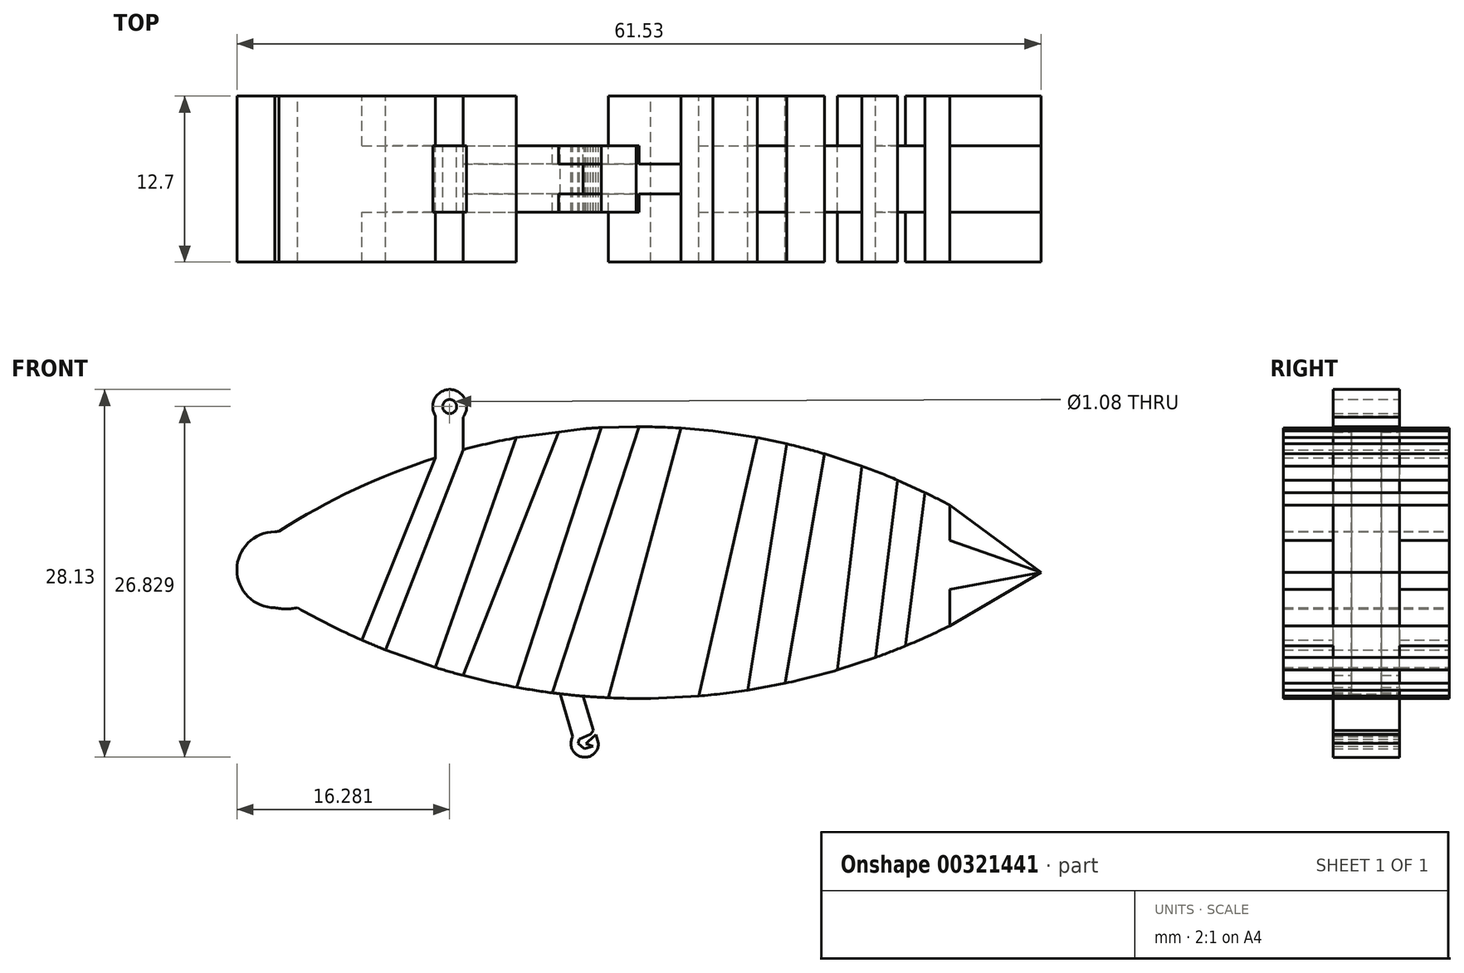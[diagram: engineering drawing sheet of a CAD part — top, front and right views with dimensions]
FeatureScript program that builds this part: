
annotation { "Feature Type Name" : "Feature", "Feature Type Description" : "" }
export const myFeature = defineFeature(function(context is Context, id is Id, definition is map)
    precondition{}
    {
        {
            var Q0;
            Q0=qCreatedBy(makeId("Front.planeOp"),FACE);
            var sketch = newSketch(context, id + "F0", { "sketchPlane" : qUnion([Q0])});
            skPoint(sketch, "E0", {"position": v(-30.3, 18.79) * mm});
            skPoint(sketch, "E1", {"position": v(21.02, 20.78) * mm});
            skArc(sketch, "E2", {"start": v(21.02, 20.78) * mm, "mid": v(-4.92, 26.75) * mm, "end": v(-30.3, 18.79) * mm});
            skPoint(sketch, "E3", {"position": v(-30.63, 18.74) * mm});
            skPoint(sketch, "E4", {"position": v(-30.63, 12.94) * mm});
            skPoint(sketch, "E5", {"position": v(-28.9, 12.94) * mm});
            skPoint(sketch, "E6", {"position": v(21.02, 11.56) * mm});
            skArc(sketch, "E7", {"start": v(-28.9, 12.94) * mm, "mid": v(-4.11, 6.01) * mm, "end": v(21.02, 11.56) * mm});
            skArc(sketch, "E8", {"start": v(-30.3, 18.79) * mm, "mid": v(-30.47, 18.77) * mm, "end": v(-30.63, 18.74) * mm});
            skArc(sketch, "E9", {"start": v(-30.63, 18.74) * mm, "mid": v(-33.53, 15.84) * mm, "end": v(-30.63, 12.94) * mm});
            skArc(sketch, "E10", {"start": v(-30.63, 12.94) * mm, "mid": v(-29.76, 12.85) * mm, "end": v(-28.9, 12.94) * mm});
            skPoint(sketch, "E11", {"position": v(28, 15.63) * mm});
            skLineSegment(sketch, "E12", {"start": v(21.02, 20.78) * mm, "end": v(28, 15.63) * mm});
            skLineSegment(sketch, "E13", {"start": v(28, 15.63) * mm, "end": v(28, 15.63) * mm});
            skLineSegment(sketch, "E14", {"start": v(28, 15.63) * mm, "end": v(21.02, 11.56) * mm});
            skPoint(sketch, "E15", {"position": v(18.72, 6.75) * mm});
            skLineSegment(sketch, "E16", {"start": v(-18.34, 24.4) * mm, "end": v(-18.34, 27.63) * mm});
            skLineSegment(sketch, "E17", {"start": v(-18.34, 27.63) * mm, "end": v(-16.23, 27.52) * mm});
            skLineSegment(sketch, "E18", {"start": v(-16.23, 27.52) * mm, "end": v(-16.23, 25.02) * mm});
            skArc(sketch, "E19", {"start": v(-16.23, 27.52) * mm, "mid": v(-17.18, 29.63) * mm, "end": v(-18.34, 27.63) * mm});
            skCircle(sketch, "E20", {"center": v(-17.25, 28.33) * mm, "radius": 0.54 * mm});
            skLineSegment(sketch, "E21", {"start": v(-23.96, 10.46) * mm, "end": v(-18.34, 24.4) * mm});
            skLineSegment(sketch, "E22", {"start": v(-16.23, 25.02) * mm, "end": v(-22.14, 9.7) * mm});
            skLineSegment(sketch, "E23", {"start": v(-22.14, 9.7) * mm, "end": v(-18.34, 8.37) * mm});
            skLineSegment(sketch, "E24", {"start": v(-18.34, 8.37) * mm, "end": v(-12.16, 25.94) * mm});
            skLineSegment(sketch, "E25", {"start": v(-12.16, 25.94) * mm, "end": v(-7.04, 26.62) * mm});
            skLineSegment(sketch, "E26", {"start": v(-16.23, 7.76) * mm, "end": v(-12.16, 6.69) * mm});
            skLineSegment(sketch, "E27", {"start": v(-12.16, 6.69) * mm, "end": v(-5.66, 26.72) * mm});
            skLineSegment(sketch, "E28", {"start": v(-5.66, 26.72) * mm, "end": v(-2.97, 26.79) * mm});
            skLineSegment(sketch, "E29", {"start": v(-7.04, 6.18) * mm, "end": v(-7.04, 6.18) * mm});
            skLineSegment(sketch, "E30", {"start": v(0, 26.72) * mm, "end": v(2.88, 26.45) * mm});
            skLineSegment(sketch, "E31", {"start": v(2.88, 26.45) * mm, "end": v(-1.88, 6) * mm});
            skLineSegment(sketch, "E32", {"start": v(-1.88, 6) * mm, "end": v(1.8, 6.18) * mm});
            skLineSegment(sketch, "E33", {"start": v(1.8, 6.18) * mm, "end": v(6.28, 25.94) * mm});
            skLineSegment(sketch, "E34", {"start": v(6.28, 25.94) * mm, "end": v(8.55, 25.47) * mm});
            skLineSegment(sketch, "E35", {"start": v(8.55, 25.47) * mm, "end": v(5.56, 6.63) * mm});
            skLineSegment(sketch, "E36", {"start": v(5.56, 6.63) * mm, "end": v(8.41, 7.16) * mm});
            skLineSegment(sketch, "E37", {"start": v(8.41, 7.16) * mm, "end": v(11.43, 24.71) * mm});
            skLineSegment(sketch, "E38", {"start": v(11.43, 24.71) * mm, "end": v(14.29, 23.78) * mm});
            skLineSegment(sketch, "E39", {"start": v(14.29, 23.78) * mm, "end": v(12.4, 8.17) * mm});
            skLineSegment(sketch, "E40", {"start": v(12.4, 8.17) * mm, "end": v(15.34, 9.13) * mm});
            skLineSegment(sketch, "E41", {"start": v(17.04, 22.7) * mm, "end": v(15.34, 9.13) * mm});
            skLineSegment(sketch, "E42", {"start": v(17.64, 10.02) * mm, "end": v(19.1, 21.75) * mm});
            skLineSegment(sketch, "E43", {"start": v(19.1, 21.75) * mm, "end": v(17.04, 22.7) * mm});
            skLineSegment(sketch, "E44", {"start": v(21.02, 20.78) * mm, "end": v(21.02, 11.56) * mm});
            skLineSegment(sketch, "E45", {"start": v(21.02, 18.09) * mm, "end": v(28, 15.63) * mm});
            skLineSegment(sketch, "E46", {"start": v(21.02, 14.33) * mm, "end": v(28, 15.63) * mm});
            skLineSegment(sketch, "E47", {"start": v(-8.79, 6.35) * mm, "end": v(-7.83, 3.08) * mm});
            skLineSegment(sketch, "E48", {"start": v(-7.83, 3.08) * mm, "end": v(-6.26, 3.54) * mm});
            skLineSegment(sketch, "E49", {"start": v(-6.26, 3.54) * mm, "end": v(-7.04, 6.18) * mm});
            skPoint(sketch, "E50", {"position": v(-5.86, 2.55) * mm});
            skArc(sketch, "E51", {"start": v(-7.83, 3.08) * mm, "mid": v(-7.18, 1.53) * mm, "end": v(-5.86, 2.55) * mm});
            skLineSegment(sketch, "E52", {"start": v(-6.28, 2.35) * mm, "end": v(-6.96, 2.15) * mm});
            skLineSegment(sketch, "E53", {"start": v(-6.96, 2.15) * mm, "end": v(-7.44, 2.55) * mm});
            skLineSegment(sketch, "E54", {"start": v(-7.44, 2.55) * mm, "end": v(-7.33, 2.9) * mm});
            skLineSegment(sketch, "E55", {"start": v(-7.33, 2.9) * mm, "end": v(-6.48, 3.25) * mm});
            skLineSegment(sketch, "E56", {"start": v(-6.48, 3.25) * mm, "end": v(-6.26, 3.54) * mm});
            skLineSegment(sketch, "E57", {"start": v(-6.06, 3.24) * mm, "end": v(-6.68, 2.7) * mm});
            skLineSegment(sketch, "E58", {"start": v(-6.68, 2.7) * mm, "end": v(-6.82, 2.54) * mm});
            skLineSegment(sketch, "E59", {"start": v(-6.82, 2.54) * mm, "end": v(-6.28, 2.35) * mm});
            skLineSegment(sketch, "E60", {"start": v(-16.23, 7.76) * mm, "end": v(-8.91, 26.37) * mm});
            skLineSegment(sketch, "E61", {"start": v(-9.4, 6.43) * mm, "end": v(-2.75, 26.79) * mm});
            skLineSegment(sketch, "E62", {"start": v(-5.1, 6.05) * mm, "end": v(0.45, 26.67) * mm});
            skLineSegment(sketch, "E63", {"start": v(-6.06, 3.24) * mm, "end": v(-5.86, 2.55) * mm});
            skSolve(sketch);
        }
        {
            var Q0;
            {var subQ0=sQuery(id+"F0.wireOp",EDGE,"E8");Q0=makeQuery(id+"F0.imprint","IMPRINT",FACE,{"disambiguationData":[TD([[makeQuery(id+"F0.imprint","IMPRINT",EDGE,{"derivedFrom":subQ0}),1.0]])]});}
            var Q1;
            {var subQ0=sQuery(id+"F0.wireOp",EDGE,"E22");Q1=makeQuery(id+"F0.imprint","IMPRINT",FACE,{"disambiguationData":[TD([[makeQuery(id+"F0.imprint","IMPRINT",EDGE,{"derivedFrom":subQ0}),1.0]])]});}
            var Q2;
            {var subQ0=sQuery(id+"F0.wireOp",EDGE,"96wlukJB-Nys0-aKYS-WkII-jcMIoTWLVjsG");Q2=makeQuery(id+"F0.imprint","IMPRINT",FACE,{"disambiguationData":[TD([[makeQuery(id+"F0.imprint","IMPRINT",EDGE,{"derivedFrom":subQ0}),1.0]])]});}
            var Q3;
            {var subQ0=sQuery(id+"F0.wireOp",EDGE,"E31");Q3=makeQuery(id+"F0.imprint","IMPRINT",FACE,{"disambiguationData":[TD([[makeQuery(id+"F0.imprint","IMPRINT",EDGE,{"derivedFrom":subQ0}),1.0]])]});}
            var Q4;
            {var subQ0=sQuery(id+"F0.wireOp",EDGE,"E35");Q4=makeQuery(id+"F0.imprint","IMPRINT",FACE,{"disambiguationData":[TD([[makeQuery(id+"F0.imprint","IMPRINT",EDGE,{"derivedFrom":subQ0}),1.0]])]});}
            var Q5;
            {var subQ0=sQuery(id+"F0.wireOp",EDGE,"E39");Q5=makeQuery(id+"F0.imprint","IMPRINT",FACE,{"disambiguationData":[TD([[makeQuery(id+"F0.imprint","IMPRINT",EDGE,{"derivedFrom":subQ0}),1.0]])]});}
            var Q6;
            {var subQ4=sQuery(id+"F0.wireOp",EDGE,"E42");Q6=makeQuery(id+"F0.imprint","IMPRINT",FACE,{"disambiguationData":[TD([[makeQuery(id+"F0.imprint","IMPRINT",EDGE,{"derivedFrom":subQ4}),-1.0]])]});}
            var Q7;
            {var subQ0=sQuery(id+"F0.wireOp",EDGE,"E45");Q7=makeQuery(id+"F0.imprint","IMPRINT",FACE,{"disambiguationData":[TD([[makeQuery(id+"F0.imprint","IMPRINT",EDGE,{"derivedFrom":subQ0}),-1.0]])]});}
            var Q8;
            {var subQ0=sQuery(id+"F0.wireOp",EDGE,"Nr8c6QaQ-9Hu6-631R-nGNs-Q67QmCpUCPg3");Q8=makeQuery(id+"F0.imprint","IMPRINT",FACE,{"disambiguationData":[TD([[makeQuery(id+"F0.imprint","IMPRINT",EDGE,{"derivedFrom":subQ0}),1.0]])]});}
            var Q9;
            {var subQ0=sQuery(id+"F0.wireOp",EDGE,"E31");Q9=makeQuery(id+"F0.imprint","IMPRINT",FACE,{"disambiguationData":[TD([[makeQuery(id+"F0.imprint","IMPRINT",EDGE,{"derivedFrom":subQ0}),-1.0]])]});}
            extrude(context, id + "F1", {"entities" : qUnion([Q0, Q1, Q2, Q3, Q4, Q5, Q6, Q7, Q8, Q9]), "endBound" : BoundingType.SYMMETRIC, "depth" : 12.7 * mm});
        }
        {
            var Q0;
            {var subQ0=sQuery(id+"F0.wireOp",EDGE,"pjh3poBZ-bAGy-p5S7-04MB-CKAZnjvh6JgX");Q0=makeQuery(id+"F0.imprint","IMPRINT",FACE,{"disambiguationData":[TD([[makeQuery(id+"F0.imprint","IMPRINT",EDGE,{"derivedFrom":subQ0}),1.0]])]});}
            var Q1;
            {var subQ3=sQuery(id+"F0.wireOp",EDGE,"e5h9nmNh-iLYF-YIr5-Ji3g-U9w3QbpzbcVt");Q1=makeQuery(id+"F0.imprint","IMPRINT",FACE,{"disambiguationData":[TD([[makeQuery(id+"F0.imprint","IMPRINT",EDGE,{"derivedFrom":subQ3}),1.0]])]});}
            var Q2;
            {var subQ3=sQuery(id+"F0.wireOp",EDGE,"27INHGbp-SGAq-Cls5-cKE2-aeLzUiNPJ58t");Q2=makeQuery(id+"F0.imprint","IMPRINT",FACE,{"disambiguationData":[TD([[makeQuery(id+"F0.imprint","IMPRINT",EDGE,{"derivedFrom":subQ3}),1.0]])]});}
            var Q3;
            {var subQ0=sQuery(id+"F0.wireOp",EDGE,"Jt77VIIY-GXs1-0jd7-35ID-bV1PNWclptak");Q3=makeQuery(id+"F0.imprint","IMPRINT",FACE,{"disambiguationData":[TD([[makeQuery(id+"F0.imprint","IMPRINT",EDGE,{"derivedFrom":subQ0}),1.0]])]});}
            var Q4;
            {var subQ3=sQuery(id+"F0.wireOp",EDGE,"E60");Q4=makeQuery(id+"F0.imprint","IMPRINT",FACE,{"disambiguationData":[TD([[makeQuery(id+"F0.imprint","IMPRINT",EDGE,{"derivedFrom":subQ3}),-1.0]])]});}
            var Q5;
            {var subQ4=sQuery(id+"F0.wireOp",EDGE,"E61");Q5=makeQuery(id+"F0.imprint","IMPRINT",FACE,{"disambiguationData":[TD([[makeQuery(id+"F0.imprint","IMPRINT",EDGE,{"derivedFrom":subQ4}),-1.0]])]});}
            var Q6;
            {var subQ0=sQuery(id+"F0.wireOp",EDGE,"E28");Q6=makeQuery(id+"F0.imprint","IMPRINT",FACE,{"disambiguationData":[TD([[makeQuery(id+"F0.imprint","IMPRINT",EDGE,{"derivedFrom":subQ0}),-1.0]])]});}
            var Q7;
            {var subQ0=sQuery(id+"F0.wireOp",EDGE,"E24");Q7=makeQuery(id+"F0.imprint","IMPRINT",FACE,{"disambiguationData":[TD([[makeQuery(id+"F0.imprint","IMPRINT",EDGE,{"derivedFrom":subQ0}),-1.0]])]});}
            var Q8;
            {var subQ0=sQuery(id+"F0.wireOp",EDGE,"E33");Q8=makeQuery(id+"F0.imprint","IMPRINT",FACE,{"disambiguationData":[TD([[makeQuery(id+"F0.imprint","IMPRINT",EDGE,{"derivedFrom":subQ0}),-1.0]])]});}
            var Q9;
            {var subQ0=sQuery(id+"F0.wireOp",EDGE,"E37");Q9=makeQuery(id+"F0.imprint","IMPRINT",FACE,{"disambiguationData":[TD([[makeQuery(id+"F0.imprint","IMPRINT",EDGE,{"derivedFrom":subQ0}),-1.0]])]});}
            var Q10;
            {var subQ0=sQuery(id+"F0.wireOp",EDGE,"E41");Q10=makeQuery(id+"F0.imprint","IMPRINT",FACE,{"disambiguationData":[TD([[makeQuery(id+"F0.imprint","IMPRINT",EDGE,{"derivedFrom":subQ0}),1.0]])]});}
            var Q11;
            {var subQ0=sQuery(id+"F0.wireOp",EDGE,"E21");Q11=makeQuery(id+"F0.imprint","IMPRINT",FACE,{"disambiguationData":[TD([[makeQuery(id+"F0.imprint","IMPRINT",EDGE,{"derivedFrom":subQ0}),-1.0]])]});}
            extrude(context, id + "F2", {"entities" : qUnion([Q0, Q1, Q2, Q3, Q4, Q5, Q6, Q7, Q8, Q9, Q10, Q11]), "operationType" : NewBodyOperationType.ADD, "endBound" : BoundingType.SYMMETRIC, "depth" : 2.3 * mm});
        }
        {
            var Q0;
            {var subQ0=sQuery(id+"F0.wireOp",EDGE,"E21");Q0=makeQuery(id+"F0.imprint","IMPRINT",FACE,{"disambiguationData":[TD([[makeQuery(id+"F0.imprint","IMPRINT",EDGE,{"derivedFrom":subQ0}),-1.0]])]});}
            var Q1;
            {var subQ0=sQuery(id+"F0.wireOp",EDGE,"E24");Q1=makeQuery(id+"F0.imprint","IMPRINT",FACE,{"disambiguationData":[TD([[makeQuery(id+"F0.imprint","IMPRINT",EDGE,{"derivedFrom":subQ0}),-1.0]])]});}
            var Q2;
            {var subQ4=sQuery(id+"F0.wireOp",EDGE,"E28");Q2=makeQuery(id+"F0.imprint","IMPRINT",FACE,{"disambiguationData":[TD([[makeQuery(id+"F0.imprint","IMPRINT",EDGE,{"derivedFrom":subQ4}),-1.0]])]});}
            var Q3;
            {var subQ0=sQuery(id+"F0.wireOp",EDGE,"E33");Q3=makeQuery(id+"F0.imprint","IMPRINT",FACE,{"disambiguationData":[TD([[makeQuery(id+"F0.imprint","IMPRINT",EDGE,{"derivedFrom":subQ0}),-1.0]])]});}
            var Q4;
            {var subQ0=sQuery(id+"F0.wireOp",EDGE,"E37");Q4=makeQuery(id+"F0.imprint","IMPRINT",FACE,{"disambiguationData":[TD([[makeQuery(id+"F0.imprint","IMPRINT",EDGE,{"derivedFrom":subQ0}),-1.0]])]});}
            var Q5;
            {var subQ1=sQuery(id+"F0.wireOp",EDGE,"E41");Q5=makeQuery(id+"F0.imprint","IMPRINT",FACE,{"disambiguationData":[TD([[makeQuery(id+"F0.imprint","IMPRINT",EDGE,{"derivedFrom":subQ1}),1.0]])]});}
            var Q6;
            {var subQ0=sQuery(id+"F0.wireOp",EDGE,"E12");Q6=makeQuery(id+"F0.imprint","IMPRINT",FACE,{"disambiguationData":[TD([[makeQuery(id+"F0.imprint","IMPRINT",EDGE,{"derivedFrom":subQ0}),-1.0]])]});}
            var Q7;
            {var subQ0=sQuery(id+"F0.wireOp",EDGE,"E14");Q7=makeQuery(id+"F0.imprint","IMPRINT",FACE,{"disambiguationData":[TD([[makeQuery(id+"F0.imprint","IMPRINT",EDGE,{"derivedFrom":subQ0}),-1.0]])]});}
            var Q8;
            {var subQ0=sQuery(id+"F0.wireOp",EDGE,"E16");Q8=makeQuery(id+"F0.imprint","IMPRINT",FACE,{"disambiguationData":[TD([[makeQuery(id+"F0.imprint","IMPRINT",EDGE,{"derivedFrom":subQ0}),-1.0]])]});}
            var Q9;
            Q9=makeQuery(id+"F0.imprint","IMPRINT",FACE,{"disambiguationData":[TD([[makeQuery(id+"F0.imprint","IMPRINT",EDGE,{"derivedFrom":sQuery(id+"F0.wireOp",EDGE,"E17")}),1.0]])]});
            var Q10;
            {var subQ2=sQuery(id+"F0.wireOp",EDGE,"E47");Q10=makeQuery(id+"F0.imprint","IMPRINT",FACE,{"disambiguationData":[TD([[makeQuery(id+"F0.imprint","IMPRINT",EDGE,{"derivedFrom":subQ2}),1.0]])]});}
            var Q11;
            Q11=makeQuery(id+"F0.imprint","IMPRINT",FACE,{"disambiguationData":[TD([[makeQuery(id+"F0.imprint","IMPRINT",EDGE,{"derivedFrom":sQuery(id+"F0.wireOp",EDGE,"E48")}),-1.0]])]});
            extrude(context, id + "F3", {"entities" : qUnion([Q0, Q1, Q2, Q3, Q4, Q5, Q6, Q7, Q8, Q9, Q10, Q11]), "operationType" : NewBodyOperationType.ADD, "endBound" : BoundingType.SYMMETRIC, "depth" : 5.08 * mm});
        }
    });
